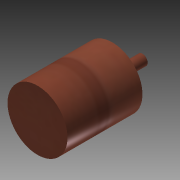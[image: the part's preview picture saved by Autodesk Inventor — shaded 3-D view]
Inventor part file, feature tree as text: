
AUTODESK INVENTOR PART (.ipt)
format: ipt  version: 2014 (Build 180170000, 170)  size: 91,648 bytes
history: native  units: mm
features: extrude x2, sketch x2, plane x1
ambient origin geometry x8: Origin, YZ Plane, XZ Plane, XY Plane, X Axis, Y Axis, Z Axis, Center Point
bodies: Solid1 (feature_tree)
feature tree (5):
  extrude  "Extrusion1"  Depth=50.0mm TaperAngle=0.0deg
  extrude  "Extrusion2"  Depth=20.0mm TaperAngle=0.0deg
  plane  "Work Plane1"
  sketch  "Sketch1"  dims[d0=40.0mm d1=50.0mm d2=0.0mm]
  sketch  "Sketch2"  dims[d3=7.0mm d4=20.0mm d5=0.0mm]
